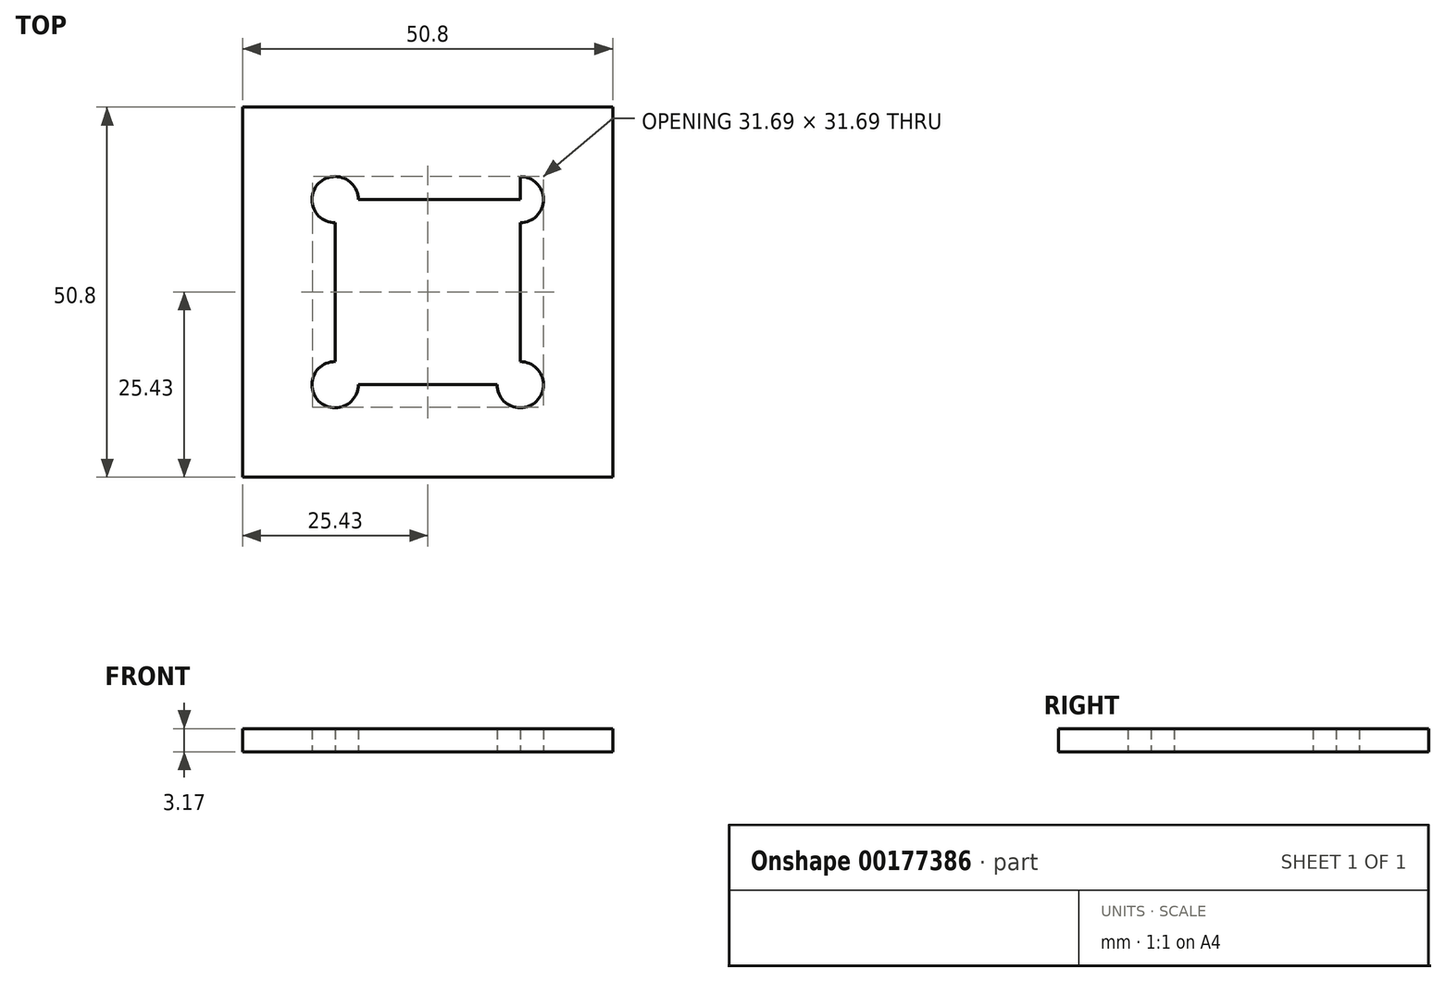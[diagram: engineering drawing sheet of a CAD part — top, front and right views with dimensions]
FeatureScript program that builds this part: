
annotation { "Feature Type Name" : "Feature", "Feature Type Description" : "" }
export const myFeature = defineFeature(function(context is Context, id is Id, definition is map)
    precondition{}
    {
        {
            var Q0;
            Q0=qCreatedBy(makeId("Top.planeOp"),FACE);
            var sketch = newSketch(context, id + "F0", { "sketchPlane" : qUnion([Q0])});
            skLineSegment(sketch, "E0.bottom", {"start": v(25.4, -25.4) * mm, "end": v(-25.4, -25.4) * mm});
            skLineSegment(sketch, "E0.top", {"start": v(25.4, 25.4) * mm, "end": v(-25.4, 25.4) * mm});
            skLineSegment(sketch, "E0.left", {"start": v(25.4, -25.4) * mm, "end": v(25.4, 25.4) * mm});
            skLineSegment(sketch, "E0.right", {"start": v(-25.4, -25.4) * mm, "end": v(-25.4, 25.4) * mm});
            skPoint(sketch, "E0.middle", {"position": v(0, 0) * mm});
            skLineSegment(sketch, "E1", {"start": v(12.7, 25.4) * mm, "end": v(12.7, -25.4) * mm});
            skLineSegment(sketch, "E2", {"start": v(-12.7, 25.4) * mm, "end": v(-12.7, -25.4) * mm});
            skLineSegment(sketch, "E3", {"start": v(-25.4, 12.7) * mm, "end": v(25.4, 12.7) * mm});
            skLineSegment(sketch, "E4", {"start": v(-25.4, -12.7) * mm, "end": v(25.4, -12.7) * mm});
            skCircle(sketch, "E5", {"center": v(-12.7, 12.7) * mm, "radius": 3.18 * mm});
            skCircle(sketch, "E6", {"center": v(12.7, 12.7) * mm, "radius": 3.18 * mm});
            skCircle(sketch, "E7", {"center": v(-12.7, -12.7) * mm, "radius": 3.18 * mm});
            skCircle(sketch, "E8", {"center": v(12.7, -12.7) * mm, "radius": 3.18 * mm});
            skSolve(sketch);
        }
        {
            var Q0;
            {var subQ1=sQuery(id+"F0.wireOp",EDGE,"E0.right");var subQ5=sQuery(id+"F0.wireOp",EDGE,"E0.top");var subQ6=makeQuery(id+"F0.imprint","INTERSECT",VERTEX,{"derivedFrom":[subQ5,subQ1]});Q0=makeQuery(id+"F0.imprint","IMPRINT",FACE,{"disambiguationData":[TD([[makeQuery(id+"F0.imprint","IMPRINT",EDGE,{"disambiguationData":[TD([[subQ6,1.0]])],"derivedFrom":subQ5}),1.0]])]});}
            var Q1;
            {var subQ7=sQuery(id+"F0.wireOp",EDGE,"E1");var subQ8=sQuery(id+"F0.wireOp",EDGE,"E0.top");var subQ9=makeQuery(id+"F0.imprint","INTERSECT",VERTEX,{"derivedFrom":[subQ8,subQ7]});Q1=makeQuery(id+"F0.imprint","IMPRINT",FACE,{"disambiguationData":[TD([[makeQuery(id+"F0.imprint","IMPRINT",EDGE,{"disambiguationData":[TD([[subQ9,-1.0]])],"derivedFrom":subQ8}),1.0]])]});}
            var Q2;
            {var subQ1=sQuery(id+"F0.wireOp",EDGE,"E0.top");var subQ5=sQuery(id+"F0.wireOp",EDGE,"E0.left");var subQ6=makeQuery(id+"F0.imprint","INTERSECT",VERTEX,{"derivedFrom":[subQ1,subQ5]});Q2=makeQuery(id+"F0.imprint","IMPRINT",FACE,{"disambiguationData":[TD([[makeQuery(id+"F0.imprint","IMPRINT",EDGE,{"disambiguationData":[TD([[subQ6,-1.0]])],"derivedFrom":subQ1}),1.0]])]});}
            var Q3;
            {var subQ1=sQuery(id+"F0.wireOp",EDGE,"E0.left");var subQ5=sQuery(id+"F0.wireOp",EDGE,"E3");var subQ6=makeQuery(id+"F0.imprint","INTERSECT",VERTEX,{"derivedFrom":[subQ1,subQ5]});Q3=makeQuery(id+"F0.imprint","IMPRINT",FACE,{"disambiguationData":[TD([[makeQuery(id+"F0.imprint","IMPRINT",EDGE,{"disambiguationData":[TD([[subQ6,1.0]])],"derivedFrom":subQ1}),1.0]])]});}
            var Q4;
            {var subQ11=sQuery(id+"F0.wireOp",EDGE,"E6");var subQ13=sQuery(id+"F0.wireOp",EDGE,"E1");var subQ14=makeQuery(id+"F0.imprint","INTERSECT",VERTEX,{"disambiguationData":[OD(1.0)],"derivedFrom":[subQ13,subQ11]});Q4=makeQuery(id+"F0.imprint","IMPRINT",FACE,{"disambiguationData":[TD([[makeQuery(id+"F0.imprint","IMPRINT",EDGE,{"disambiguationData":[TD([[subQ14,-1.0]])],"derivedFrom":subQ13}),-1.0]])]});}
            var Q5;
            {var subQ1=sQuery(id+"F0.wireOp",EDGE,"E0.right");var subQ9=sQuery(id+"F0.wireOp",EDGE,"E3");var subQ10=makeQuery(id+"F0.imprint","INTERSECT",VERTEX,{"derivedFrom":[subQ1,subQ9]});Q5=makeQuery(id+"F0.imprint","IMPRINT",FACE,{"disambiguationData":[TD([[makeQuery(id+"F0.imprint","IMPRINT",EDGE,{"disambiguationData":[TD([[subQ10,1.0]])],"derivedFrom":subQ1}),-1.0]])]});}
            var Q6;
            {var subQ1=sQuery(id+"F0.wireOp",EDGE,"E0.bottom");var subQ5=sQuery(id+"F0.wireOp",EDGE,"E0.right");var subQ6=makeQuery(id+"F0.imprint","INTERSECT",VERTEX,{"derivedFrom":[subQ1,subQ5]});Q6=makeQuery(id+"F0.imprint","IMPRINT",FACE,{"disambiguationData":[TD([[makeQuery(id+"F0.imprint","IMPRINT",EDGE,{"disambiguationData":[TD([[subQ6,1.0]])],"derivedFrom":subQ1}),-1.0]])]});}
            var Q7;
            {var subQ6=sQuery(id+"F0.wireOp",EDGE,"E0.bottom");var subQ9=sQuery(id+"F0.wireOp",EDGE,"E1");var subQ10=makeQuery(id+"F0.imprint","INTERSECT",VERTEX,{"derivedFrom":[subQ6,subQ9]});Q7=makeQuery(id+"F0.imprint","IMPRINT",FACE,{"disambiguationData":[TD([[makeQuery(id+"F0.imprint","IMPRINT",EDGE,{"disambiguationData":[TD([[subQ10,-1.0]])],"derivedFrom":subQ6}),-1.0]])]});}
            var Q8;
            {var subQ0=sQuery(id+"F0.wireOp",EDGE,"E0.left");var subQ1=sQuery(id+"F0.wireOp",EDGE,"E0.bottom");var subQ2=makeQuery(id+"F0.imprint","INTERSECT",VERTEX,{"derivedFrom":[subQ1,subQ0]});Q8=makeQuery(id+"F0.imprint","IMPRINT",FACE,{"disambiguationData":[TD([[makeQuery(id+"F0.imprint","IMPRINT",EDGE,{"disambiguationData":[TD([[subQ2,-1.0]])],"derivedFrom":subQ1}),-1.0]])]});}
            extrude(context, id + "F1", {"entities" : qUnion([Q0, Q1, Q2, Q3, Q4, Q5, Q6, Q7, Q8]), "depth" : 3.17 * mm});
        }
    });
